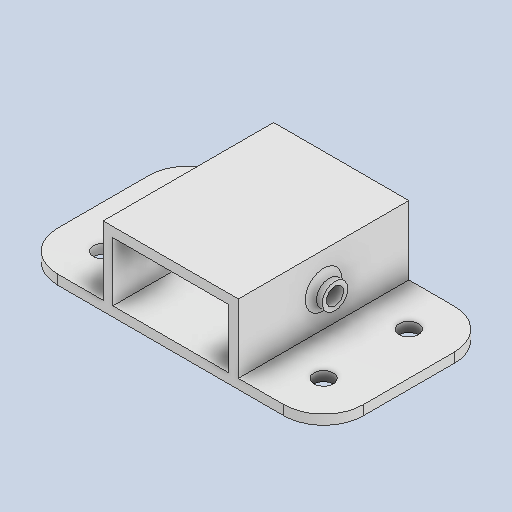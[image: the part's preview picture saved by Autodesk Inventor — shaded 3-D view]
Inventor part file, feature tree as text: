
AUTODESK INVENTOR PART (.ipt)
format: ipt  version: 2023 (Build 270158000, 158)  size: 304,128 bytes
history: native  units: mm
features: extrude x4, sketch x4, fillet x2, hole x1, mirror x1
ambient origin geometry x8: Origin, YZ Plane, XZ Plane, XY Plane, X Axis, Y Axis, Z Axis, Center Point
bodies: Solid1 (feature_tree)
feature tree (12):
  extrude  "Extrusion1"  Depth=10.4mm
  extrude  "Extrusion2"  Depth=30.0mm TaperAngle=0.0deg
  hole  "Hole1"  [1 undecoded]
  mirror  "Mirror1"
  fillet  "Fillet1"  Radius=7.0mm
  sketch  "Sketch4"  dims[d8=3.4mm d9=6.0mm d10=4.0mm d11=2.0mm d12=90.0deg d13=5.0mm d14=20.594885mm d15=7.0mm d16=3.0mm d17=0.75mm d18=2.0mm d19=0.0mm d20=1.0mm d21=2.0mm d22=0.0mm d23=30.0mm d24=7.5mm d25=7.5mm]
  extrude  "Extrusion3"  Depth=30.0mm
  fillet  "Fillet2"  Radius=0.75mm
  extrude  "Extrusion4"  Depth=2.0mm TaperAngle=0.0deg
  sketch  "Sketch1"  dims[d0=20.4mm d1=10.4mm]
  sketch  "Sketch2"  dims[d2=1.7mm d3=30.0mm d4=0.0mm]
  sketch  "Sketch3"  dims[d5=53.8mm d6=1.7mm d7=0.0mm]
note: 1 required parameter value undecoded (feature->parameter linkage not recoverable at this tier; creation-order binding heuristic only, values carry confidence <= 0.55)
